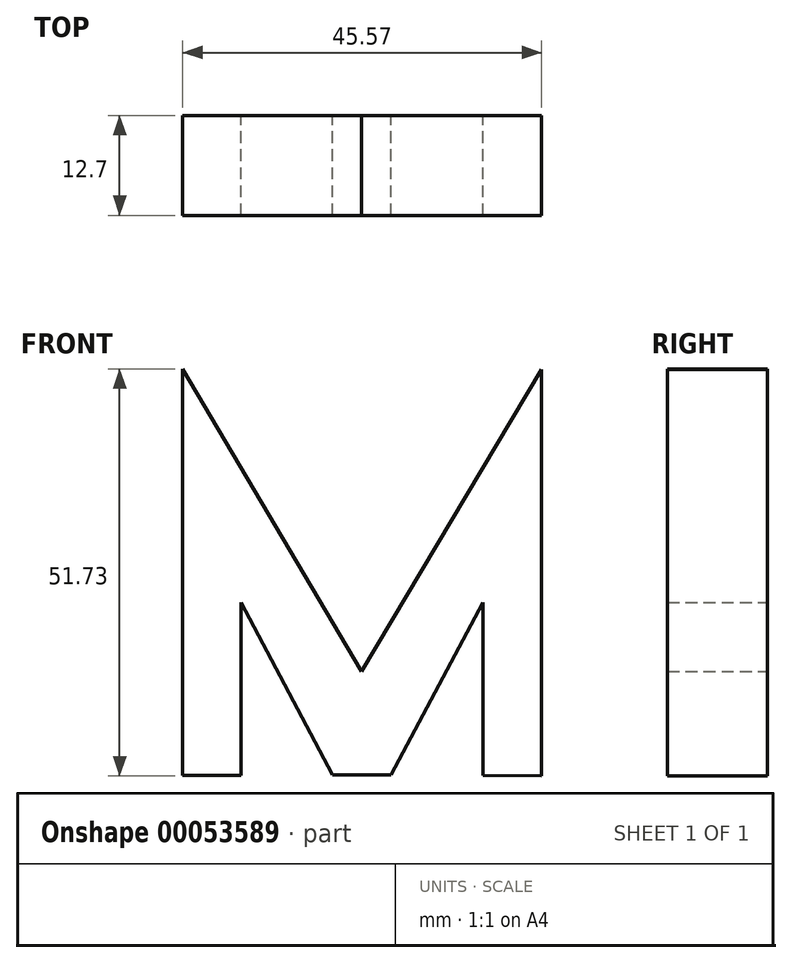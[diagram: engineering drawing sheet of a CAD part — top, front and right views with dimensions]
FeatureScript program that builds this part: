
annotation { "Feature Type Name" : "Feature", "Feature Type Description" : "" }
export const myFeature = defineFeature(function(context is Context, id is Id, definition is map)
    precondition{}
    {
        {
            var Q0;
            Q0=qCreatedBy(makeId("Front.planeOp"),FACE);
            var sketch = newSketch(context, id + "F0", { "sketchPlane" : qUnion([Q0])});
            skLineSegment(sketch, "E0", {"start": v(-36.58, 29.7) * mm, "end": v(-36.58, -21.95) * mm});
            skLineSegment(sketch, "E1", {"start": v(8.99, -22.03) * mm, "end": v(8.99, 29.62) * mm});
            skLineSegment(sketch, "E2", {"start": v(-36.58, 29.7) * mm, "end": v(-13.87, -8.71) * mm});
            skLineSegment(sketch, "E3", {"start": v(-13.87, -8.71) * mm, "end": v(8.99, 29.62) * mm});
            skLineSegment(sketch, "E4", {"start": v(-29.16, -21.95) * mm, "end": v(-29.16, 0) * mm});
            skLineSegment(sketch, "E5", {"start": v(-29.16, 0) * mm, "end": v(-17.58, -21.87) * mm});
            skLineSegment(sketch, "E6", {"start": v(-17.58, -21.87) * mm, "end": v(-10.16, -21.87) * mm});
            skLineSegment(sketch, "E7", {"start": v(-10.16, -21.87) * mm, "end": v(1.56, 0) * mm});
            skLineSegment(sketch, "E8", {"start": v(1.56, 0) * mm, "end": v(1.56, -21.95) * mm});
            skLineSegment(sketch, "E9", {"start": v(1.56, -21.95) * mm, "end": v(8.99, -22.03) * mm});
            skLineSegment(sketch, "E10", {"start": v(-36.58, -21.95) * mm, "end": v(-29.16, -21.95) * mm});
            skPoint(sketch, "E11.endSnap0", {"position": v(-12.01, -15.3) * mm});
            skSolve(sketch);
        }
        {
            var Q0;
            Q0 = qSketchRegion(id + "F0", true);
            extrude(context, id + "F1", {"entities" : qUnion([Q0]), "depth" : 12.7 * mm});
        }
    });
